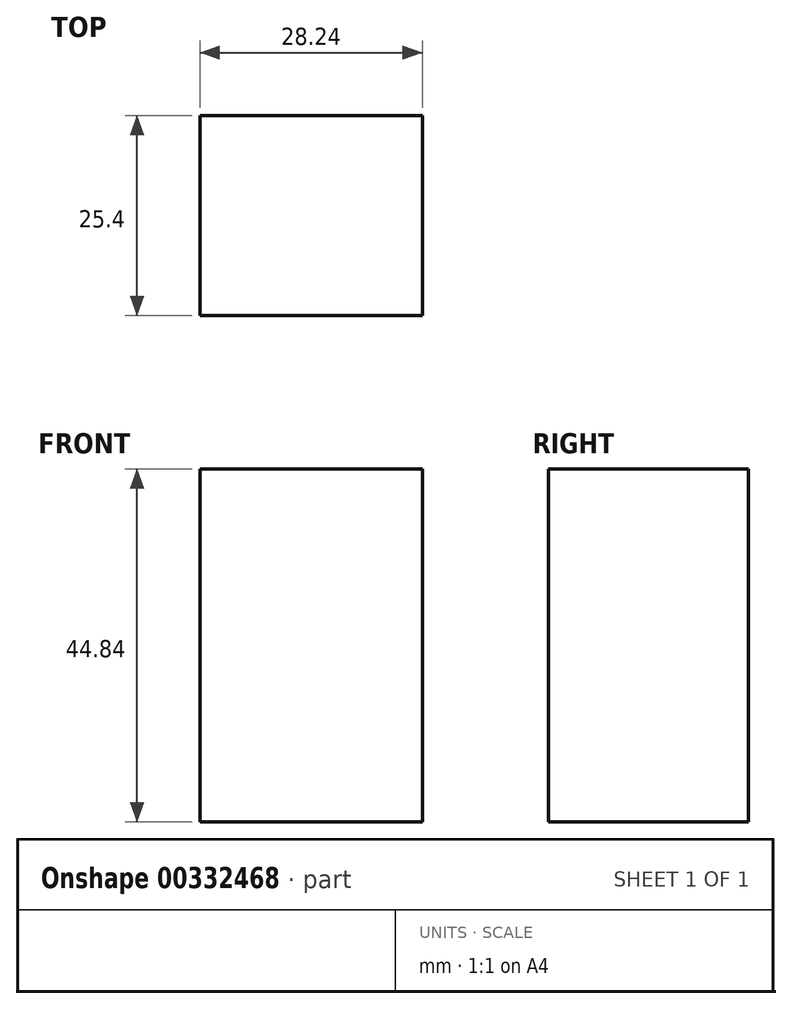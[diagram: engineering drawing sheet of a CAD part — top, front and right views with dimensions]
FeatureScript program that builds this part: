
annotation { "Feature Type Name" : "Feature", "Feature Type Description" : "" }
export const myFeature = defineFeature(function(context is Context, id is Id, definition is map)
    precondition{}
    {
        {
            var Q0;
            Q0=qCreatedBy(makeId("Front.planeOp"),FACE);
            var sketch = newSketch(context, id + "F0", { "sketchPlane" : qUnion([Q0])});
            skLineSegment(sketch, "E0.bottom", {"start": v(14.12, 22.42) * mm, "end": v(-14.12, 22.42) * mm});
            skLineSegment(sketch, "E0.top", {"start": v(14.12, -22.42) * mm, "end": v(-14.12, -22.42) * mm});
            skLineSegment(sketch, "E0.left", {"start": v(14.12, 22.42) * mm, "end": v(14.12, -22.42) * mm});
            skLineSegment(sketch, "E0.right", {"start": v(-14.12, 22.42) * mm, "end": v(-14.12, -22.42) * mm});
            skPoint(sketch, "E0.middle", {"position": v(0, 0) * mm});
            skSolve(sketch);
        }
        {
            var Q0;
            Q0=makeQuery(id+"F0.imprint","IMPRINT",FACE,{"disambiguationData":[TD([[makeQuery(id+"F0.imprint","IMPRINT",EDGE,{"derivedFrom":sQuery(id+"F0.wireOp",EDGE,"E0.bottom")}),1.0]])]});
            extrude(context, id + "F1", {"entities" : qUnion([Q0]), "endBound" : BoundingType.SYMMETRIC, "depth" : 25.4 * mm});
        }
    });
